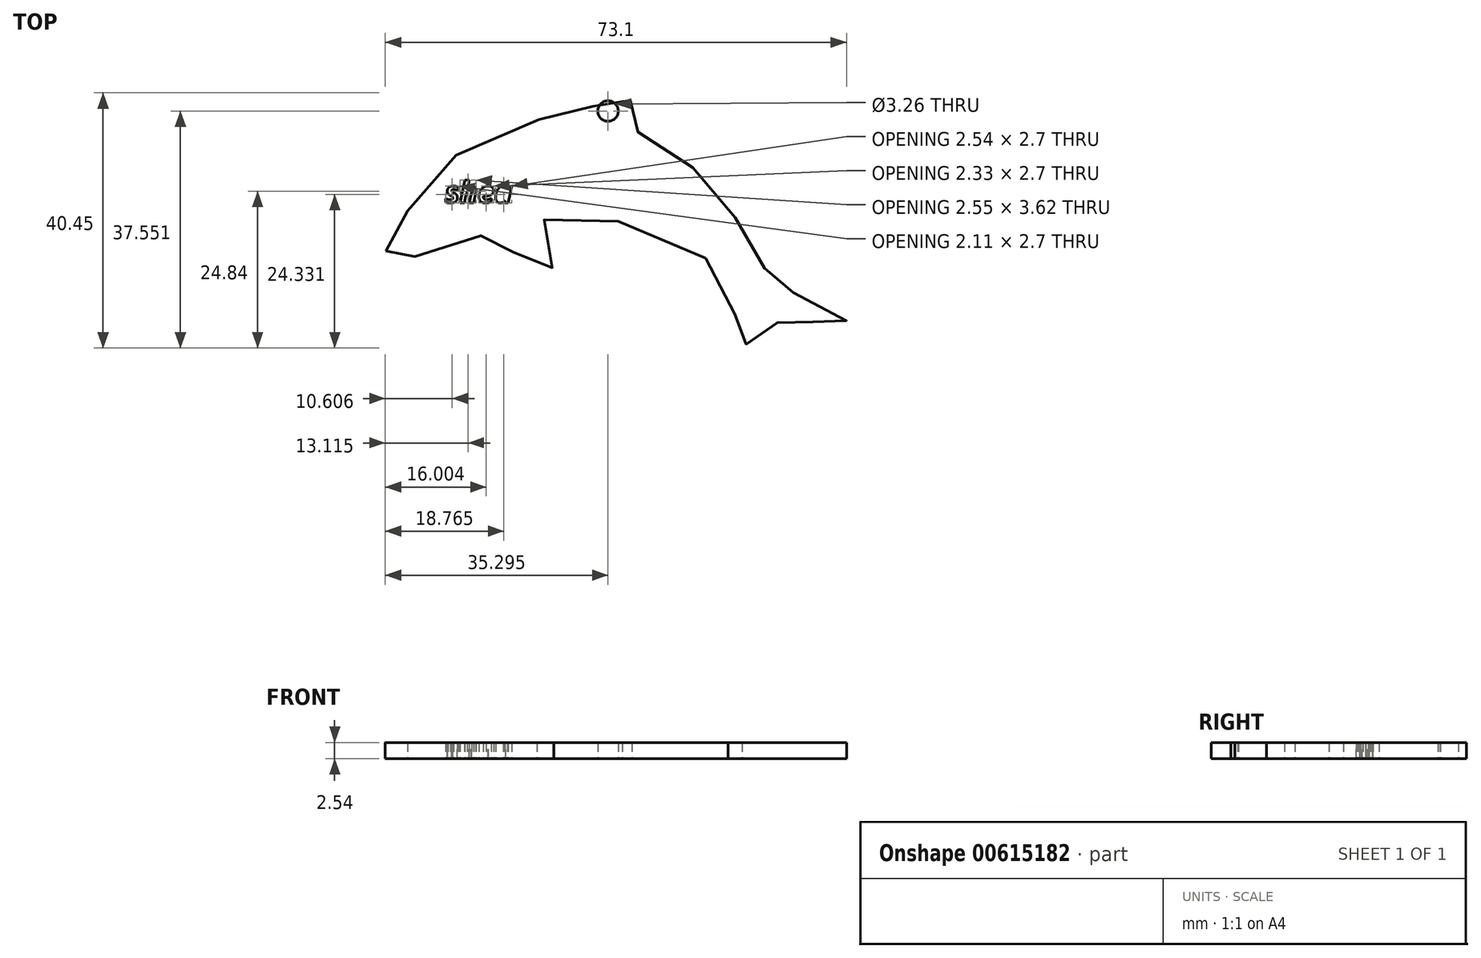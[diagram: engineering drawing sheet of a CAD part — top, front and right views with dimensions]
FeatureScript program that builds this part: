
annotation { "Feature Type Name" : "Feature", "Feature Type Description" : "" }
export const myFeature = defineFeature(function(context is Context, id is Id, definition is map)
    precondition{}
    {
        {
            var Q0;
            Q0=qCreatedBy(makeId("Top.planeOp"),FACE);
            var sketch = newSketch(context, id + "F0", { "sketchPlane" : qUnion([Q0])});
            skFitSpline(sketch, "E0", {"points": [v(0.74, -28.1) * mm, v(3.9, -24.72) * mm, v(4.29, -20.86) * mm, v(11.86, -12.97) * mm, v(25.33, -7.22) * mm, v(31.56, -6.83) * mm, v(36.21, -3.28) * mm, v(39.76, -3.67) * mm, v(38.42, -5.49) * mm, v(39.05, -8.32) * mm, v(42.6, -9.98) * mm, v(49.92, -15.42) * mm, v(55.13, -21.49) * mm, v(58.67, -26.69) * mm, v(61.27, -31.97) * mm, v(62.93, -34.57) * mm, v(66.48, -34.8) * mm, v(73.5, -38.51) * mm, v(73.57, -39.7) * mm, v(72.07, -39.38) * mm, v(68.13, -39.46) * mm, v(65.85, -40.32) * mm, v(63, -39.3) * mm, v(62.06, -40.4) * mm, v(59.3, -41.2) * mm, v(56.94, -43.48) * mm, v(55.05, -39.77) * mm, v(57.18, -36.38) * mm, v(47.24, -26.53) * mm, v(33.69, -22.9) * mm, v(25.41, -23.46) * mm, v(25.41, -28.1) * mm, v(27.3, -31.57) * mm, v(22.81, -30.4) * mm, v(18.63, -24.88) * mm, v(17.45, -25.2) * mm, v(10.91, -26.77) * mm, v(3.5, -29.76) * mm, v(1.37, -30) * mm, v(0.74, -28.1) * mm]});
            skText(sketch, "E1", { "text": "shea ", "fontName": "OpenSans-BoldItalic.ttf"});
            skCircle(sketch, "E2", {"center": v(35.94, -5.93) * mm, "radius": 1.63 * mm});
            const initialGuessF0  = {"E1": [0.01015, -0.02045, 1, 0, 0.00343]};
            skSetInitialGuess(sketch, initialGuessF0);
            skSolve(sketch);
        }
        {
            var Q0;
            Q0=makeQuery(id+"F0.imprint","IMPRINT",FACE,{"disambiguationData":[TD([[makeQuery(id+"F0.imprint","IMPRINT",EDGE,{"derivedFrom":sQuery(id+"F0.wireOp",EDGE,"E0")}),-1.0]])]});
            extrude(context, id + "F1", {"entities" : qUnion([Q0]), "depth" : 2.54 * mm, "offsetDistance" : 25.4 * mm});
        }
    });
